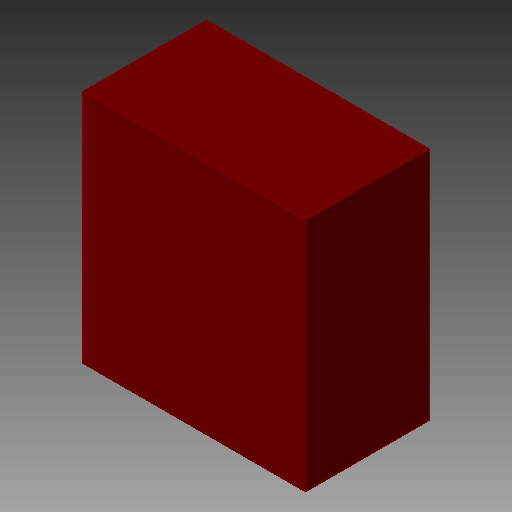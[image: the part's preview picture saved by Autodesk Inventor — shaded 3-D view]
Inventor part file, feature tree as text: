
AUTODESK INVENTOR PART (.ipt)
format: ipt  version: 2018 (Build 220112000, 112)  size: 80,384 bytes
history: native  units: in
note: dims shown in document units (in); Inventor stores cm internally (conversion verified against a paired STEP export)
features: other x1, extrude x1
ambient origin geometry x8: Origin, YZ Plane, XZ Plane, XY Plane, X Axis, Y Axis, Z Axis, Center Point
bodies: Solid1 (feature_tree)
feature tree (2):
  other  "TPD2E001-DRL, TPD2E001DRLR_175"
  extrude  "Extrusion1"  Depth=0.0394in TaperAngle=0.0deg
